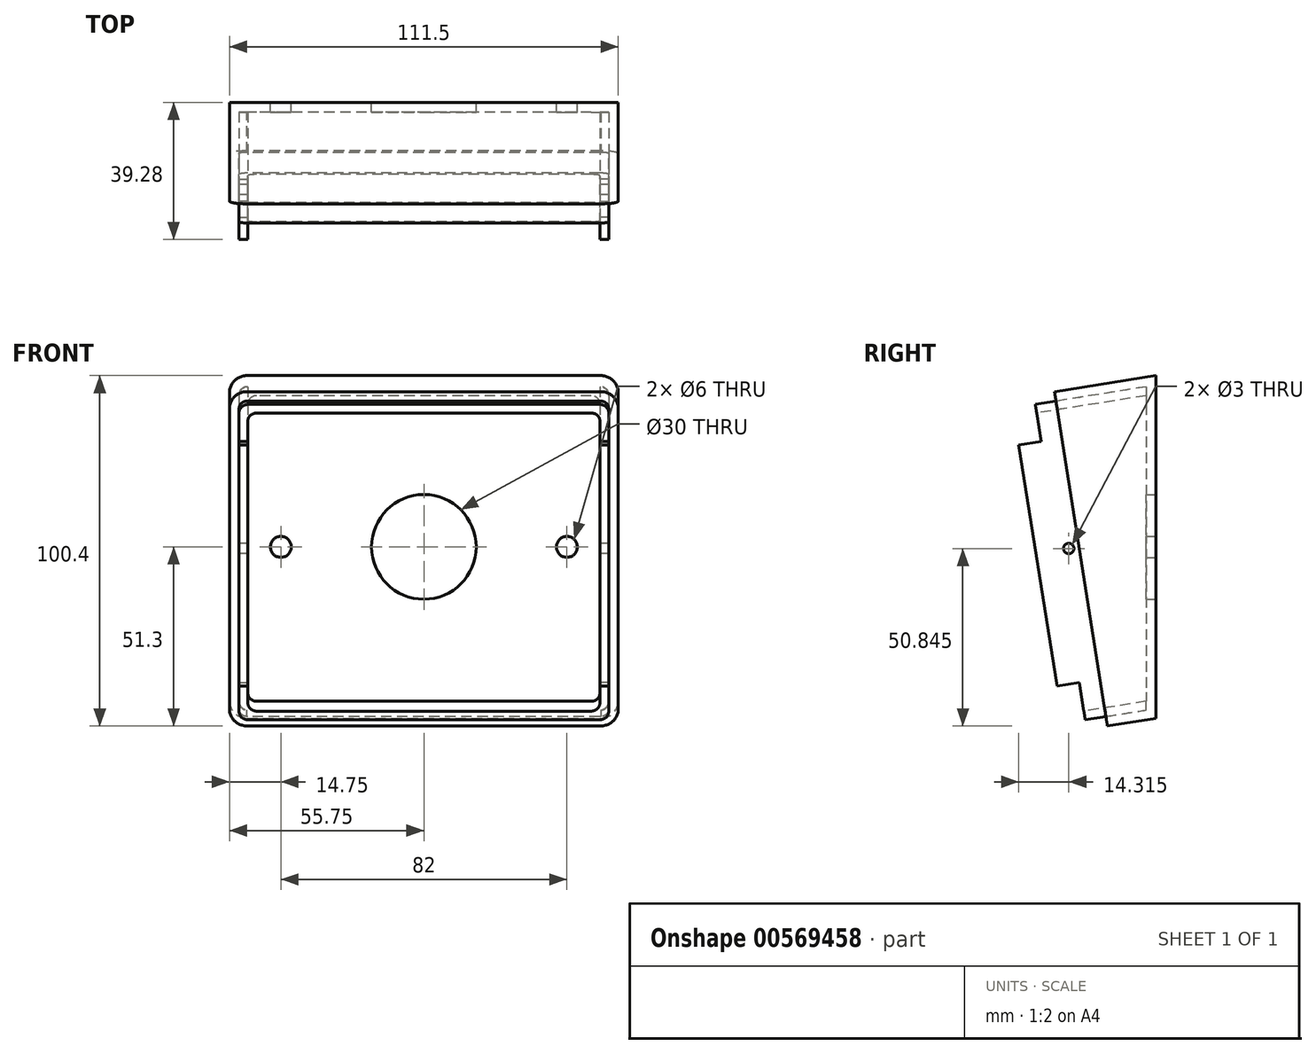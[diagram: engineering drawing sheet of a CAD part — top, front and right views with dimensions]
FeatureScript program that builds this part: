
annotation { "Feature Type Name" : "Feature", "Feature Type Description" : "" }
export const myFeature = defineFeature(function(context is Context, id is Id, definition is map)
    precondition{}
    {
        {
            var Q0;
            Q0=qCreatedBy(makeId("Front.planeOp"),FACE);
            cPlane(context, id + "F0", {"entities" : qUnion([Q0]), "cplaneType" : CPlaneType.OFFSET, "offset" : 22 * mm, "width" : 150 * mm, "height" : 150 * mm});
        }
        {
            var Q0;
            Q0=qCreatedBy(id+"F0.planeOp",FACE);
            var sketch = newSketch(context, id + "F1", { "sketchPlane" : qUnion([Q0])});
            skLineSegment(sketch, "E0", {"start": v(-67.43, 0) * mm, "end": v(64.52, 0) * mm});
            skSolve(sketch);
        }
        {
            var Q0;
            Q0=qCreatedBy(makeId("Front.planeOp"),FACE);
            var Q1;
            Q1=sQuery(id+"F1.wireOp",EDGE,"E0");
            cPlane(context, id + "F2", {"entities" : qUnion([Q0, Q1]), "cplaneType" : CPlaneType.LINE_ANGLE, "offset" : 15 * mm, "angle" : 9 * degree, "width" : 150 * mm, "height" : 150 * mm});
        }
        {
            var Q0;
            Q0=qCreatedBy(id+"F2.planeOp",FACE);
            var sketch = newSketch(context, id + "F3", { "sketchPlane" : qUnion([Q0])});
            skLineSegment(sketch, "E1.bottom", {"start": v(-50.75, 48.5) * mm, "end": v(50.75, 48.5) * mm});
            skLineSegment(sketch, "E1.top", {"start": v(-50.75, -48.5) * mm, "end": v(50.75, -48.5) * mm});
            skLineSegment(sketch, "E1.left", {"start": v(-55.75, 43.5) * mm, "end": v(-55.75, -43.5) * mm});
            skLineSegment(sketch, "E1.right", {"start": v(55.75, 43.5) * mm, "end": v(55.75, -43.5) * mm});
            skPoint(sketch, "E1.middle", {"position": v(0, 0) * mm});
            skPoint(sketch, "E2.visualSharp", {"position": v(-55.75, 48.5) * mm});
            skArc(sketch, "E2.filletArc", {"start": v(-50.75, 48.5) * mm, "mid": v(-54.29, 47.04) * mm, "end": v(-55.75, 43.5) * mm});
            skPoint(sketch, "E3.visualSharp", {"position": v(55.75, 48.5) * mm});
            skArc(sketch, "E3.filletArc", {"start": v(55.75, 43.5) * mm, "mid": v(54.29, 47.04) * mm, "end": v(50.75, 48.5) * mm});
            skPoint(sketch, "E4.visualSharp", {"position": v(55.75, -48.5) * mm});
            skArc(sketch, "E4.filletArc", {"start": v(50.75, -48.5) * mm, "mid": v(54.29, -47.04) * mm, "end": v(55.75, -43.5) * mm});
            skPoint(sketch, "E5.visualSharp", {"position": v(-55.75, -48.5) * mm});
            skArc(sketch, "E5.filletArc", {"start": v(-55.75, -43.5) * mm, "mid": v(-54.29, -47.04) * mm, "end": v(-50.75, -48.5) * mm});
            skSolve(sketch);
        }
        {
            var Q0;
            Q0=qSketchRegion(id+"F3",true);
            var Q1;
            Q1=qCreatedBy(makeId("Front.planeOp"),FACE);
            extrude(context, id + "F4", {"entities" : qUnion([Q0]), "endBound" : BoundingType.UP_TO_SURFACE, "endBoundEntityFace" : qUnion([Q1]), "depth" : 20 * mm, "offsetDistance" : 25 * mm});
        }
        {
            var Q0;
            Q0=makeQuery(id+"F4.opExtrude","CAP_FACE",FACE,{"disambiguationData":[OSD([sQuery(id+"F3.wireOp",EDGE,"E1.bottom"),sQuery(id+"F3.wireOp",EDGE,"E1.top"),sQuery(id+"F3.wireOp",EDGE,"E1.left"),sQuery(id+"F3.wireOp",EDGE,"E1.right"),sQuery(id+"F3.wireOp",EDGE,"E2.filletArc"),sQuery(id+"F3.wireOp",EDGE,"E3.filletArc"),sQuery(id+"F3.wireOp",EDGE,"E4.filletArc"),sQuery(id+"F3.wireOp",EDGE,"E5.filletArc")])],"isStart":true});
            shell(context, id + "F5", {"entities" : qUnion([Q0]), "thickness" : 2.75 * mm});
        }
        {
            var Q0;
            Q0=qCreatedBy(makeId("Front.planeOp"),FACE);
            var sketch = newSketch(context, id + "F6", { "sketchPlane" : qUnion([Q0])});
            skCircle(sketch, "E6", {"center": v(0, 0) * mm, "radius": 15 * mm});
            skCircle(sketch, "E7", {"center": v(-41, 0) * mm, "radius": 3 * mm});
            skCircle(sketch, "E8.MirrorC", {"center": v(41, 0) * mm, "radius": 3 * mm});
            skSolve(sketch);
        }
        {
            var Q0;
            Q0 = qSketchRegion(id + "F6", true);
            extrude(context, id + "F7", {"entities" : qUnion([Q0]), "operationType" : NewBodyOperationType.REMOVE, "depth" : 25 * mm, "offsetDistance" : 25 * mm});
        }
        {
            var Q0;
            Q0=qCreatedBy(id+"F2.planeOp",FACE);
            cPlane(context, id + "F8", {"entities" : qUnion([Q0]), "cplaneType" : CPlaneType.OFFSET, "offset" : 6 * mm, "oppositeDirection" : true, "width" : 150 * mm, "height" : 150 * mm});
        }
        {
            var Q0;
            Q0=qCreatedBy(id+"F8.planeOp",FACE);
            var sketch = newSketch(context, id + "F9", { "sketchPlane" : qUnion([Q0])});
            skLineSegment(sketch, "E9.bottom", {"start": v(-50.5, 45.74) * mm, "end": v(50.5, 45.74) * mm});
            skLineSegment(sketch, "E9.top", {"start": v(-50.5, -45.76) * mm, "end": v(50.5, -45.76) * mm});
            skLineSegment(sketch, "E9.left", {"start": v(-53, 43.24) * mm, "end": v(-53, -43.26) * mm});
            skLineSegment(sketch, "E9.right", {"start": v(53, 43.24) * mm, "end": v(53, -43.26) * mm});
            skPoint(sketch, "E9.middle", {"position": v(0, 0) * mm});
            skPoint(sketch, "E10.visualSharp", {"position": v(-53, 45.74) * mm});
            skArc(sketch, "E10.filletArc", {"start": v(-50.5, 45.74) * mm, "mid": v(-52.27, 45) * mm, "end": v(-53, 43.24) * mm});
            skPoint(sketch, "E11.visualSharp", {"position": v(53, 45.74) * mm});
            skArc(sketch, "E11.filletArc", {"start": v(53, 43.24) * mm, "mid": v(52.27, 45) * mm, "end": v(50.5, 45.74) * mm});
            skPoint(sketch, "E12.visualSharp", {"position": v(53, -45.76) * mm});
            skArc(sketch, "E12.filletArc", {"start": v(50.5, -45.76) * mm, "mid": v(52.27, -45.03) * mm, "end": v(53, -43.26) * mm});
            skPoint(sketch, "E13.visualSharp", {"position": v(-53, -45.76) * mm});
            skArc(sketch, "E13.filletArc", {"start": v(-53, -43.26) * mm, "mid": v(-52.27, -45.03) * mm, "end": v(-50.5, -45.76) * mm});
            skLineSegment(sketch, "E14.bottom", {"start": v(-48, 43.24) * mm, "end": v(48, 43.24) * mm});
            skLineSegment(sketch, "E14.top", {"start": v(-48, -43.26) * mm, "end": v(48, -43.26) * mm});
            skLineSegment(sketch, "E14.left", {"start": v(-50.5, 40.74) * mm, "end": v(-50.5, -40.76) * mm});
            skLineSegment(sketch, "E14.right", {"start": v(50.5, 40.74) * mm, "end": v(50.5, -40.76) * mm});
            skArc(sketch, "E15.filletArc", {"start": v(-48, 43.24) * mm, "mid": v(-49.77, 42.5) * mm, "end": v(-50.5, 40.74) * mm});
            skArc(sketch, "E16.filletArc", {"start": v(50.5, 40.74) * mm, "mid": v(49.77, 42.5) * mm, "end": v(48, 43.24) * mm});
            skArc(sketch, "E17.filletArc", {"start": v(48, -43.26) * mm, "mid": v(49.77, -42.53) * mm, "end": v(50.5, -40.76) * mm});
            skArc(sketch, "E18.filletArc", {"start": v(-50.5, -40.76) * mm, "mid": v(-49.77, -42.53) * mm, "end": v(-48, -43.26) * mm});
            skSolve(sketch);
        }
        {
            var Q0;
            Q0 = qSketchRegion(id + "F9", true);
            var Q1;
            Q1=qCreatedBy(makeId("Front.planeOp"),FACE);
            extrude(context, id + "F10", {"entities" : qUnion([Q0]), "operationType" : NewBodyOperationType.ADD, "endBound" : BoundingType.UP_TO_SURFACE, "depth" : 25 * mm, "endBoundEntityFace" : qUnion([Q1]), "offsetDistance" : 25 * mm});
        }
        {
            var Q0;
            Q0=qCreatedBy(id+"F2.planeOp",FACE);
            cPlane(context, id + "F11", {"entities" : qUnion([Q0]), "cplaneType" : CPlaneType.OFFSET, "offset" : 12.5 * mm, "oppositeDirection" : true, "width" : 150 * mm, "height" : 150 * mm});
        }
        {
            var Q0;
            Q0=qCreatedBy(makeId("Front.planeOp"),FACE);
            cPlane(context, id + "F12", {"entities" : qUnion([Q0]), "cplaneType" : CPlaneType.OFFSET, "offset" : 2.5 * mm, "width" : 150 * mm, "height" : 150 * mm});
        }
        {
            var Q0;
            Q0=sQuery(id+"F1.wireOp",EDGE,"E0");
            cPlane(context, id + "F13", {"entities" : qUnion([Q0]), "cplaneType" : CPlaneType.LINE_ANGLE, "offset" : 25 * mm, "angle" : 81 * degree, "oppositeDirection" : true, "width" : 150 * mm, "height" : 150 * mm});
        }
        {
            var Q0;
            Q0=qCreatedBy(id+"F11.planeOp",FACE);
            var sketch = newSketch(context, id + "F14", { "sketchPlane" : qUnion([Q0])});
            skLineSegment(sketch, "E19.bottom", {"start": v(50.5, 35) * mm, "end": v(53, 35) * mm});
            skLineSegment(sketch, "E19.top", {"start": v(50.5, -35) * mm, "end": v(53, -35) * mm});
            skLineSegment(sketch, "E19.left", {"start": v(50.5, 35) * mm, "end": v(50.5, -35) * mm});
            skLineSegment(sketch, "E19.right", {"start": v(53, 35) * mm, "end": v(53, -35) * mm});
            skPoint(sketch, "E19.middle", {"position": v(51.75, 0) * mm});
            skLineSegment(sketch, "E20.MirrorCS", {"start": v(-53, 35) * mm, "end": v(-53, -35) * mm});
            skLineSegment(sketch, "E21.MirrorCS", {"start": v(-50.5, 35) * mm, "end": v(-50.5, -35) * mm});
            skLineSegment(sketch, "E22.MirrorCS", {"start": v(-50.5, 35) * mm, "end": v(-53, 35) * mm});
            skLineSegment(sketch, "E23.MirrorCS", {"start": v(-50.5, -35) * mm, "end": v(-53, -35) * mm});
            skSolve(sketch);
        }
        {
            var Q0;
            Q0 = qSketchRegion(id + "F14", true);
            var Q1;
            Q1=qCreatedBy(makeId("Front.planeOp"),FACE);
            extrude(context, id + "F15", {"entities" : qUnion([Q0]), "operationType" : NewBodyOperationType.ADD, "endBound" : BoundingType.UP_TO_SURFACE, "depth" : 25 * mm, "endBoundEntityFace" : qUnion([Q1]), "offsetDistance" : 25 * mm});
        }
        {
            var Q0;
            Q0=qCreatedBy(makeId("Right.planeOp"),FACE);
            var sketch = newSketch(context, id + "F16", { "sketchPlane" : qUnion([Q0])});
            skCircle(sketch, "E24", {"center": v(-24.97, -0.46) * mm, "radius": 1.5 * mm});
            skSolve(sketch);
        }
        {
            var Q0;
            Q0 = qSketchRegion(id + "F16", true);
            extrude(context, id + "F17", {"entities" : qUnion([Q0]), "operationType" : NewBodyOperationType.REMOVE, "endBound" : BoundingType.SYMMETRIC, "depth" : 140 * mm, "offsetDistance" : 25 * mm});
        }
    });
